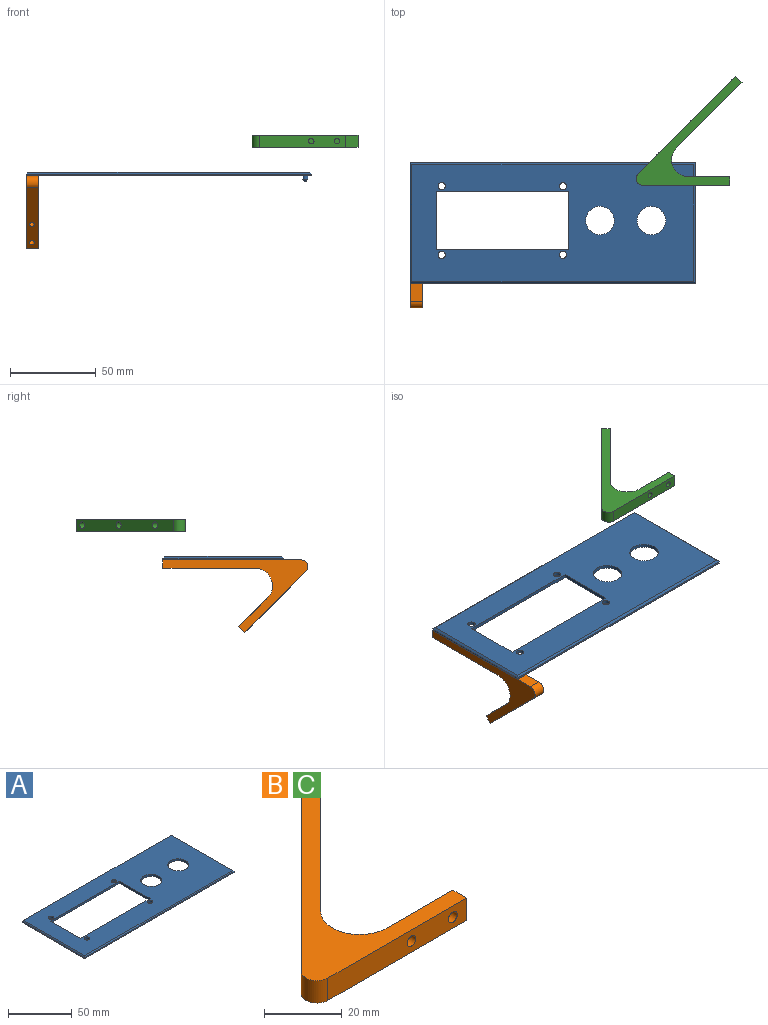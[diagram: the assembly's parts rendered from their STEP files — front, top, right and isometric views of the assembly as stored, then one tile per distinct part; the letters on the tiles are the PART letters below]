
ASSEMBLY  parts=3 mates=1
PART A: 38 faces, bbox 166x70x5 mm
  f0: plane 164x68mm, normal (0,0,1), area 8089.4mm2, adj f6,f7,f8,f9,f10,f11,f12,f13
  f1: plane 166x70mm, normal (0,0,-1), area 8515mm2, adj f2,f3,f4,f5,f6,f7,f8,f9
  f2: plane 166x1mm, normal (0,1,0), area 166mm2, adj f1,f3,f5,f37
  f3: plane 70x1mm, normal (-1,0,0), area 70mm2, adj f1,f2,f4,f35
  f4: plane 166x1mm, normal (0,-1,0), area 166mm2, adj f1,f3,f5,f34
  f5: plane 70x1mm, normal (1,0,0), area 70mm2, adj f1,f2,f4,f36
  f6: plane 77x2mm, normal (0,1,0), area 154mm2, adj f0,f1,f7,f8
  f7: plane 33.5x2mm, normal (1,0,0), area 67mm2, adj f0,f1,f6,f9
  f8: plane 33.5x2mm, normal (-1,0,0), area 67mm2, adj f0,f1,f6,f9
  f9: plane 77x2mm, normal (0,-1,0), area 154mm2, adj f0,f1,f7,f8
  f10: cylinder r=2.1mm len=4.2mm, axis (0,0,1), area 26.4mm2, adj f0,f1
  f11: cylinder r=2.1mm len=4.2mm, axis (0,0,1), area 26.4mm2, adj f0,f1
  f12: cylinder r=2.1mm len=4.2mm, axis (0,0,1), area 26.4mm2, adj f0,f1
  f13: cylinder r=2.1mm len=4.2mm, axis (0,0,1), area 26.4mm2, adj f0,f1
  f14: cylinder r=8.25mm len=16.5mm, axis (0,0,1), area 103.7mm2, adj f0,f1
  f15: cylinder r=8.25mm len=16.5mm, axis (0,0,1), area 103.7mm2, adj f0,f1
  f16: cylinder r=1.5mm len=3mm, axis (0,0,1), area 18.8mm2, adj f1,f32
  f17: plane 1x1mm, normal (0,0,-1), area 0.8mm2, adj f32
  f18: cylinder r=1.5mm len=3mm, axis (0,0,1), area 18.8mm2, adj f1,f33
  f19: plane 1x1mm, normal (0,0,-1), area 0.8mm2, adj f33
  f20: cylinder r=1.5mm len=3mm, axis (0,0,1), area 18.8mm2, adj f1,f31
  f21: plane 1x1mm, normal (0,0,-1), area 0.8mm2, adj f31
  f22: cylinder r=1.5mm len=3mm, axis (0,0,1), area 18.8mm2, adj f1,f30
  f23: plane 1x1mm, normal (0,0,-1), area 0.8mm2, adj f30
  f24: cylinder r=1.5mm len=3mm, axis (0,0,1), area 18.8mm2, adj f1,f28
  f25: plane 1x1mm, normal (0,0,-1), area 0.8mm2, adj f28
  f26: cylinder r=1.5mm len=3mm, axis (0,0,1), area 18.8mm2, adj f1,f29
  f27: plane 1x1mm, normal (0,0,-1), area 0.8mm2, adj f29
  f28: cone r=0.5mm half-angle=45deg, axis (0,0,1), area 8.9mm2, adj f24,f25
  f29: cone r=0.5mm half-angle=45deg, axis (0,0,1), area 8.9mm2, adj f26,f27
  f30: cone r=1.5mm half-angle=45deg, axis (0,0,1), area 8.9mm2, adj f22,f23
  f31: cone r=0.5mm half-angle=45deg, axis (0,0,1), area 8.9mm2, adj f20,f21
  f32: cone r=1.5mm half-angle=45deg, axis (0,0,1), area 8.9mm2, adj f16,f17
  f33: cone r=1.5mm half-angle=45deg, axis (0,0,1), area 8.9mm2, adj f18,f19
  f34: plane 166x1mm, normal (0,-0.71,0.71), area 233.3mm2, adj f0,f4,f35,f36
  f35: plane 70x1mm, normal (-0.71,0,0.71), area 97.6mm2, adj f0,f3,f34,f37
  f36: plane 70x1mm, normal (0.71,0,0.71), area 97.6mm2, adj f0,f5,f34,f37
  f37: plane 166x1mm, normal (0,0.71,0.71), area 233.3mm2, adj f0,f2,f35,f36
PART B: 18 faces, bbox 61.5x63.6x7 mm
  f0: plane 56.81x56.81mm, normal (-0.71,0.71,0), area 524.7mm2, adj f3,f4,f8,f9,f11,f13,f15
  f1: cylinder r=10mm len=17.07mm, axis (0,0,-1), area 164.9mm2, adj f2,f7,f8,f9
  f2: plane 38.03x38.03mm, normal (0.71,-0.71,0), area 376.5mm2, adj f1,f3,f8,f9
  f3: plane 7x3.54mm, normal (0.71,0.71,0), area 35mm2, adj f0,f2,f8,f9
  f4: cylinder r=4mm len=7mm, axis (0,0,-1), area 66mm2, adj f0,f5,f8,f9
  f5: plane 50.34x7mm, normal (0,-1,0), area 336.3mm2, adj f4,f6,f8,f9,f16,f17
  f6: plane 7x5mm, normal (1,0,0), area 35mm2, adj f5,f7,f8,f9
  f7: plane 23.79x7mm, normal (0,1,0), area 150.4mm2, adj f1,f6,f8,f9,f16,f17
  f8: plane 63.64x61.52mm, normal (0,0,1), area 793.5mm2, adj f0,f1,f2,f3,f4,f5,f6,f7
  f9: plane 63.64x61.52mm, normal (0,0,-1), area 793.5mm2, adj f0,f1,f2,f3,f4,f5,f6,f7
  f10: plane 4x2.83mm, normal (-0.71,0.71,0), area 12.6mm2, adj f11
  f11: cylinder r=2mm len=5.66mm, axis (-0.71,0.71,0), area 50.3mm2, adj f0,f10
  f12: plane 4x2.83mm, normal (-0.71,0.71,0), area 12.6mm2, adj f13
  f13: cylinder r=2mm len=5.66mm, axis (-0.71,0.71,0), area 50.3mm2, adj f0,f12
  f14: plane 4x2.83mm, normal (-0.71,0.71,0), area 12.6mm2, adj f15
  f15: cylinder r=2mm len=5.66mm, axis (-0.71,0.71,0), area 50.3mm2, adj f0,f14
  f16: cylinder r=1.6mm len=5mm, axis (0,1,0), area 50.3mm2, adj f5,f7
  f17: cylinder r=1.6mm len=5mm, axis (0,1,0), area 50.3mm2, adj f5,f7
PART C: same geometry as B
PLACE A t=(-77.81,-21.91,-16.64)mm
PLACE B rot(axis=(0.36,0.86,0.36),98.4deg) t=(-160.81,-52.28,-41.26)mm
PLACE C at identity
MATE fastened B.f11 <-> A.f16  axis (0,0,1) through (-157.31,-21.91,-16.64)mm
